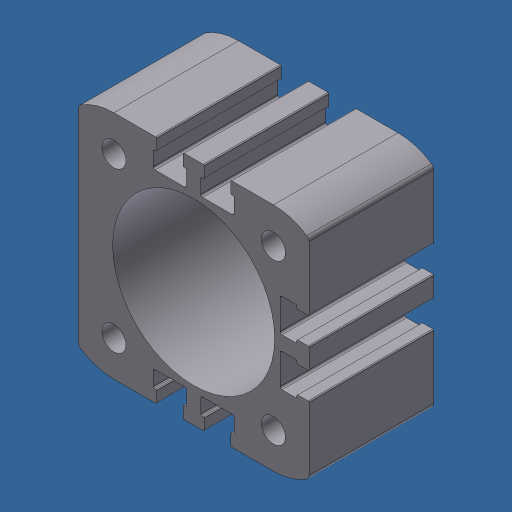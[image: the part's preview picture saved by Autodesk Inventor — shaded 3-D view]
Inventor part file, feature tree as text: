
AUTODESK INVENTOR PART (.ipt)
format: ipt  version: 2024.3 (Build 283343000, 343)  size: 300,544 bytes
history: native  units: mm (DEFAULTED — no unit token found)
features: other x1, sketch x1, extrude x1, hole x1
ambient origin geometry x8: Origin, YZ Plane, XZ Plane, XY Plane, X Axis, Y Axis, Z Axis, Center Point
bodies: Body1 (feature_tree)
feature tree (4):
  other  "Finish - None"
  sketch  "Sketch1"  dims[d0=25.4mm d1=0.0mm d2=33.0mm d3=4.91mm d4=12.7mm d5=9.525mm d6=6.35mm d7=14.3117mm d8=19.05mm d9=20.594885mm]
  extrude  "FESTO, 32MM"  Depth=19.05mm
  hole  "Hole1"  [1 undecoded]
note: 1 required parameter value undecoded (feature->parameter linkage not recoverable at this tier; creation-order binding heuristic only, values carry confidence <= 0.55)
